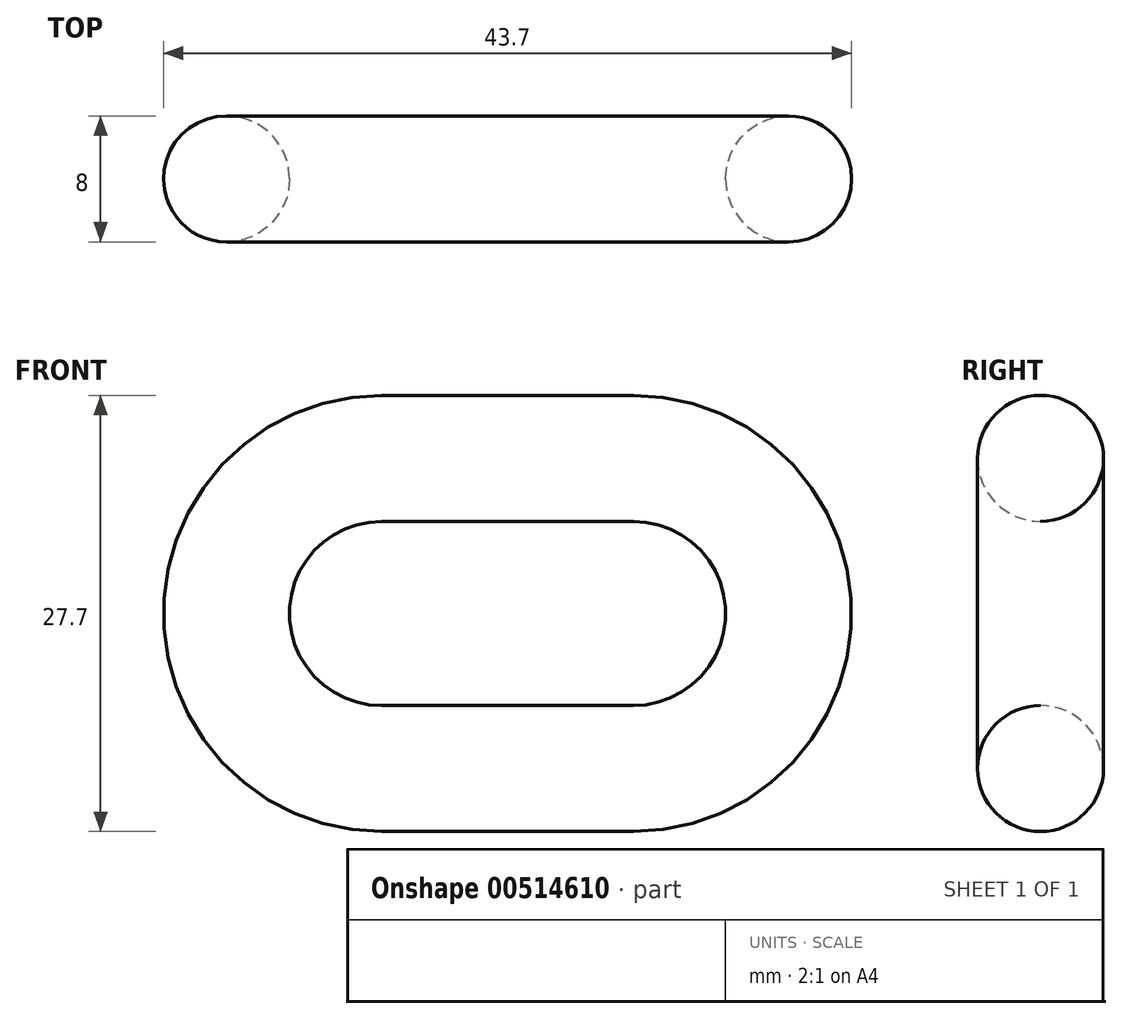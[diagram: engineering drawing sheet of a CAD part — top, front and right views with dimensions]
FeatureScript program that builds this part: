
annotation { "Feature Type Name" : "Feature", "Feature Type Description" : "" }
export const myFeature = defineFeature(function(context is Context, id is Id, definition is map)
    precondition{}
    {
        {
            var Q0;
            Q0=qCreatedBy(makeId("Front.planeOp"),FACE);
            var sketch = newSketch(context, id + "F0", { "sketchPlane" : qUnion([Q0])});
            skArc(sketch, "E0", {"start": v(-8, 9.85) * mm, "mid": v(-17.85, 0) * mm, "end": v(-8, -9.85) * mm});
            skArc(sketch, "E1.MirrorCS", {"start": v(8, 9.85) * mm, "mid": v(17.85, 0) * mm, "end": v(8, -9.85) * mm});
            skLineSegment(sketch, "E2", {"start": v(-8, 9.85) * mm, "end": v(8, 9.85) * mm});
            skLineSegment(sketch, "E3", {"start": v(-8, -9.85) * mm, "end": v(8, -9.85) * mm});
            skSolve(sketch);
        }
        {
            var Q0;
            Q0=qCreatedBy(makeId("Right.planeOp"),FACE);
            cPlane(context, id + "F1", {"entities" : qUnion([Q0]), "cplaneType" : CPlaneType.OFFSET, "offset" : 8 * mm, "oppositeDirection" : true, "width" : 150 * mm, "height" : 150 * mm});
        }
        {
            var Q0;
            Q0=qCreatedBy(id+"F1.planeOp",FACE);
            var sketch = newSketch(context, id + "F2", { "sketchPlane" : qUnion([Q0])});
            skCircle(sketch, "E4", {"center": v(0, 9.85) * mm, "radius": 4 * mm});
            skSolve(sketch);
        }
        {
            var Q0;
            Q0=makeQuery(id+"F2.imprint","IMPRINT",FACE,{"disambiguationData":[TD([[makeQuery(id+"F2.imprint","IMPRINT",EDGE,{"derivedFrom":sQuery(id+"F2.wireOp",EDGE,"E4")}),1.0]])]});
            var Q1;
            Q1=sQuery(id+"F0.wireOp",EDGE,"E0");
            var Q2;
            Q2=sQuery(id+"F0.wireOp",EDGE,"E3");
            var Q3;
            Q3=sQuery(id+"F0.wireOp",EDGE,"E1.MirrorCS");
            var Q4;
            Q4=sQuery(id+"F0.wireOp",EDGE,"E2");
            sweep(context, id + "F3", {"profiles" : qUnion([Q0]), "path" : qUnion([Q1, Q2, Q3, Q4])});
        }
    });
